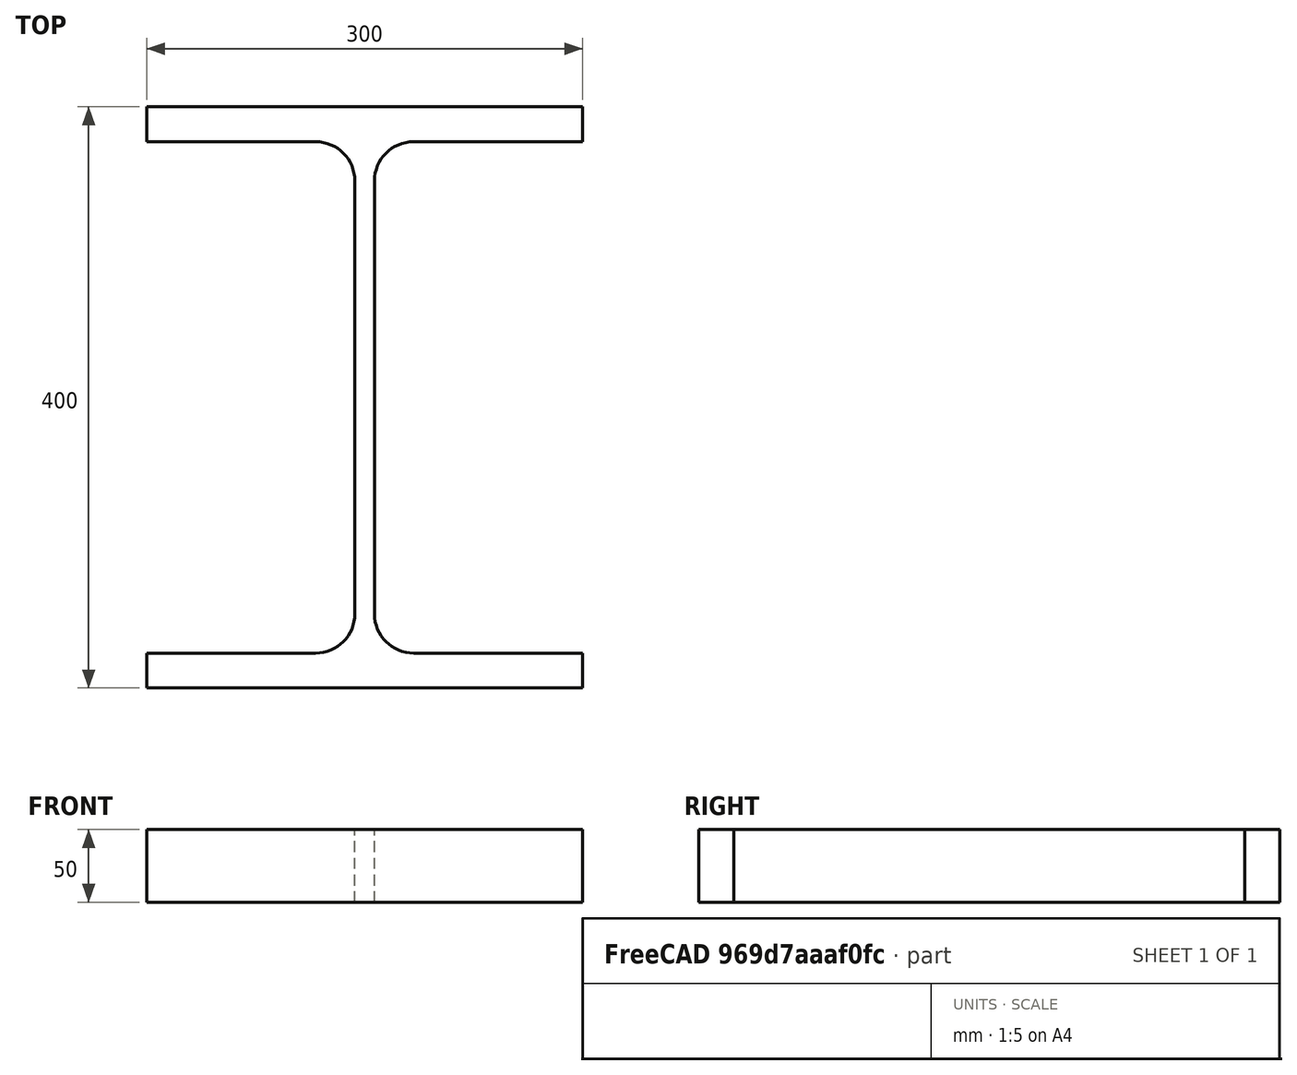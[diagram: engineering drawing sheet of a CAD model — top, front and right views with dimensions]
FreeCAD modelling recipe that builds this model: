
FCSTD DOCUMENT  (FreeCAD 0.15R4671 (Git))
Label: HE-B-Profile 400 DIN1025-2 S235JR
License: All rights reserved
LicenseURL: http://en.wikipedia.org/wiki/All_rights_reserved
objects: Sketcher::SketchObject×1, Part::Extrusion×1
note: 2 computed .brp shape members not serialized (recipe doc carries the construction recipe); baked Part::Feature solids carry a one-line shape summary decoded from their .brp

FEATURE [Sketcher::SketchObject] Sketch
  sketch-geometry (16):
    g0: LineSegment StartX=6.75 StartY=-149 StartZ=0 EndX=6.75 EndY=149 EndZ=0
    g1: LineSegment StartX=33.75 StartY=176 StartZ=0 EndX=150 EndY=176 EndZ=0
    g2: LineSegment StartX=150 StartY=176 StartZ=0 EndX=150 EndY=200 EndZ=0
    g3: LineSegment StartX=150 StartY=200 StartZ=0 EndX=-150 EndY=200 EndZ=0
    g4: LineSegment StartX=-150 StartY=200 StartZ=0 EndX=-150 EndY=176 EndZ=0
    g5: LineSegment StartX=-150 StartY=176 StartZ=0 EndX=-33.75 EndY=176 EndZ=0
    g6: LineSegment StartX=-6.75 StartY=149 StartZ=0 EndX=-6.75 EndY=-149 EndZ=0
    g7: LineSegment StartX=-33.75 StartY=-176 StartZ=0 EndX=-150 EndY=-176 EndZ=0
    g8: LineSegment StartX=-150 StartY=-176 StartZ=0 EndX=-150 EndY=-200 EndZ=0
    g9: LineSegment StartX=-150 StartY=-200 StartZ=0 EndX=150 EndY=-200 EndZ=0
    g10: LineSegment StartX=150 StartY=-200 StartZ=0 EndX=150 EndY=-176 EndZ=0
    g11: LineSegment StartX=150 StartY=-176 StartZ=0 EndX=33.75 EndY=-176 EndZ=0
    g12: ArcOfCircle CenterX=33.75 CenterY=149 CenterZ=0 NormalX=0 NormalY=0 NormalZ=1 Radius=27 StartAngle=1.5708 EndAngle=3.14159
    g13: ArcOfCircle CenterX=33.75 CenterY=-149 CenterZ=0 NormalX=0 NormalY=0 NormalZ=1 Radius=27 StartAngle=3.14159 EndAngle=4.71239
    g14: ArcOfCircle CenterX=-33.75 CenterY=149 CenterZ=0 NormalX=0 NormalY=0 NormalZ=1 Radius=27 StartAngle=0 EndAngle=1.5708
    g15: ArcOfCircle CenterX=-33.75 CenterY=-149 CenterZ=0 NormalX=0 NormalY=0 NormalZ=1 Radius=27 StartAngle=4.71239 EndAngle=6.28319
  constraints (42):
    c: Vertical(g0)
    c: Coincident(g2,g1)
    c: Vertical(g2)
    c: Coincident(g3,g2)
    c: Coincident(g4,g3)
    c: Vertical(g4)
    c: Coincident(g5,g4)
    c: Horizontal(g5)
    c: Vertical(g6)
    c: Horizontal(g7)
    c: Coincident(g8,g7)
    c: Vertical(g8)
    c: Coincident(g9,g8)
    c: Horizontal(g9)
    c: Coincident(g10,g9)
    c: Vertical(g10)
    c: Coincident(g11,g10)
    c: Horizontal(g11)
    c: Tangent(g1,g12) = 1.5708
    c: Tangent(g0,g12) = 1.5708
    c: Tangent(g0,g13) = 1.5708
    c: Tangent(g11,g13) = 1.5708
    c: Tangent(g5,g14) = 1.5708
    c: Tangent(g6,g14) = 1.5708
    c: Tangent(g6,g15) = 1.5708
    c: Tangent(g7,g15) = 1.5708
    c: Equal(g3,g9)
    c: Equal(g2,g4)
    c: Equal(g4,g8)
    c: Equal(g8,g10)
    c: Equal(g12,g14)
    c: Equal(g14,g15)
    c: Equal(g15,g13)
    c: Symmetric(g2,g3,g-2)
    c: Symmetric(g9,g8,g-2)
    c: Symmetric(g0,g6,g-2)
    c: Symmetric(g2,g9,g-1)
    c: DistanceY(g2,g9) = -400
    c: DistanceX(g3) = -300
    c: DistanceX(g0,g6) = -13.5
    c: DistanceY(g2) = 24
    c: Radius(g12) = 27
FEATURE [Part::Extrusion] Extrude  label="HE-B-Profile 400 DIN1025-2 S235JR"
  Base = -> Sketch
  Dir = (0,0,50)
  Solid = true
